# Revit family: 26603GN0_26545GN0_28417GN0_26635GN0
name_source: partatom
category: Plumbing Fixtures
revit_build: Autodesk Revit 2015 (Build: 20140606_1530(x64)
units: mm (PartAtom-declared; Revit-internal decimal feet)

## types (1)
- 26603GN0
    Assembly Code = D2010710
    CWFU = 3
    Cold Water Connection Diameter = 1/2"
    Cold Water Connection Radius = 1/4"
    Default Elevation = 78"
    Description = Rainshower SmartActive 36" Shower Bar
    Finish = Metal-Grohe-GN0-Brushed Cool Sunrise
    HWFU = 3
    Height = 36"
    Hot Water Connection Diameter = 1"
    Hot Water Connection Radius = 1/4"
    Installation Type = Wall Mounted
    Label = Ceiling Rain Shower/Wall Mounted Head Shower/Hand Shower
    Length = 3 3/16"
    Manufacturer = Grohe
    Material = Metal-Grohe-GN0-Brushed Cool Sunrise
    Model = 26603GN0
    Price = Prices may vary. Please consult Manufacturer Representative for most up-to-date price list.
    Product Page URL = https://www.grohe.us
    Shower Elbow Specification = GROHE 26635GN0 Shower outlet elbow 13 mm (1/2") NPT female thread inlet Protected against backflow GROHE Hard Graphite finish
    Shower Hose Specification = GROHE 28417GN0 Shower Hose 59" (1499 mm) Metal Rotation cone for twist-free function GROHE Hard Graphite finish
    Tempered Connection Diameter = 1/2"
    Tempered Connection Radius = 1/4"
    URL = https://www.grohe.us
    Vacuum Breaker Specification = GROHE 07911GN0 1/2" In-Line Vacuum Breaker Installed between supply outlet and shower hose GROHE Starlight® finish
    Vent Connection = No
    WFU = 4
    Warranty Documentation Link = https://cdn.cloud.grohe.com
    Waste Connection = No
    Width = 2 7/8"
    cUPC Compliant = Yes

## geometry (parser evidence)
native form markers: Sweep x5
no freeform markers — native parametric forms only
